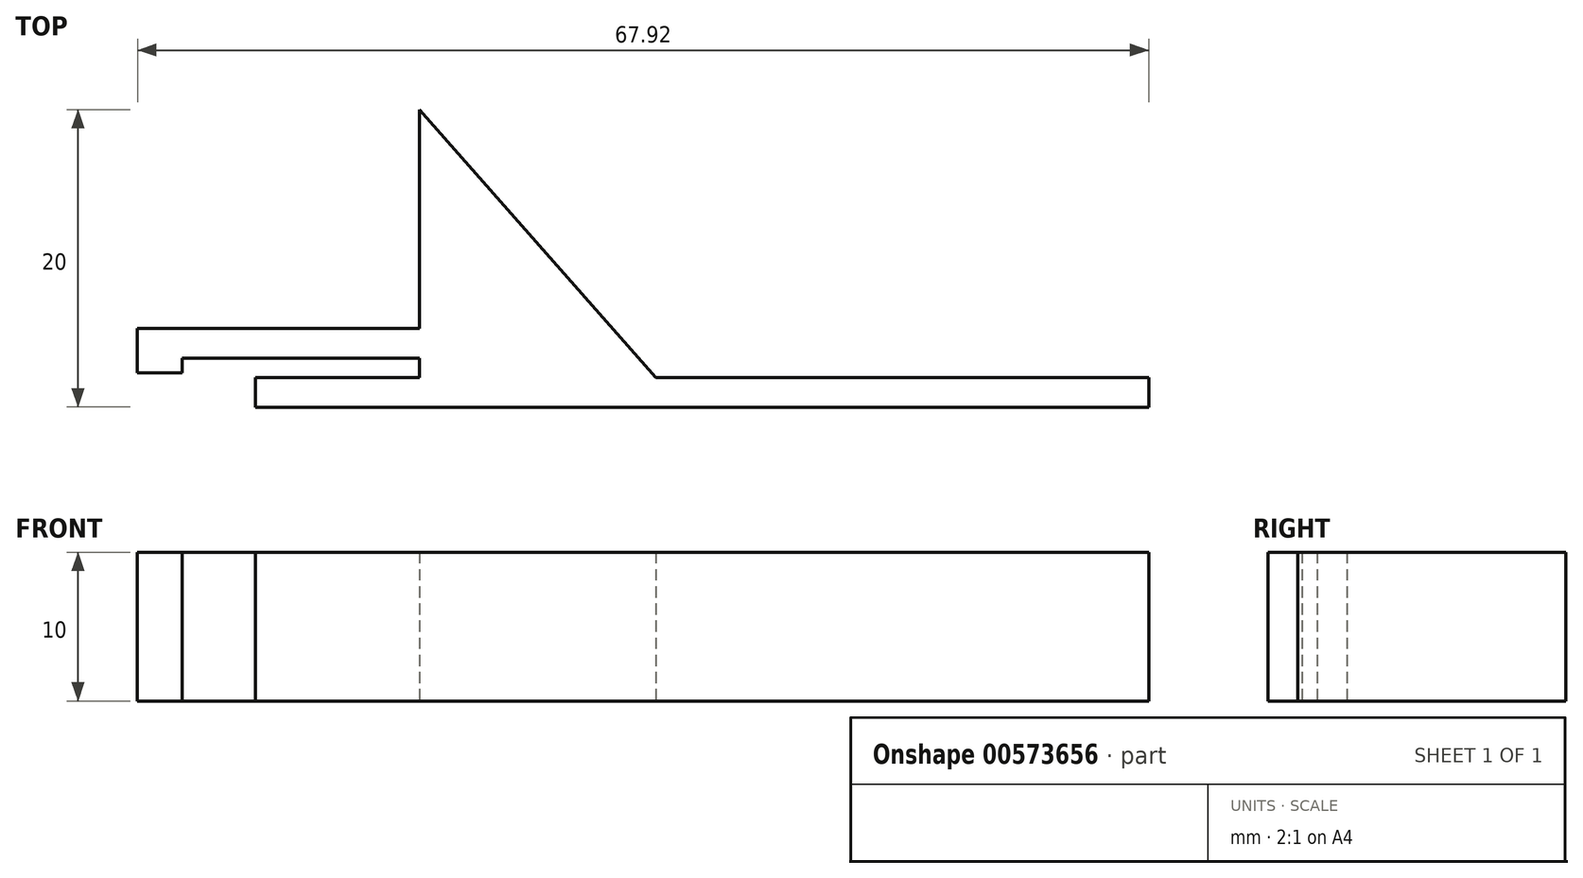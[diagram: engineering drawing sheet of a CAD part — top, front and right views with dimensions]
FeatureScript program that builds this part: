
annotation { "Feature Type Name" : "Feature", "Feature Type Description" : "" }
export const myFeature = defineFeature(function(context is Context, id is Id, definition is map)
    precondition{}
    {
        {
            var Q0;
            Q0=qCreatedBy(makeId("Top.planeOp"),FACE);
            var sketch = newSketch(context, id + "F0", { "sketchPlane" : qUnion([Q0])});
            skLineSegment(sketch, "E0", {"start": v(-11, 1.8) * mm, "end": v(49, 1.8) * mm});
            skLineSegment(sketch, "E1", {"start": v(49, 1.8) * mm, "end": v(49, 3.8) * mm});
            skLineSegment(sketch, "E2", {"start": v(49.2, 3.8) * mm, "end": v(15.9, 3.8) * mm});
            skLineSegment(sketch, "E3", {"start": v(-11, 1.8) * mm, "end": v(-11, 3.8) * mm});
            skLineSegment(sketch, "E4", {"start": v(-11, 3.8) * mm, "end": v(0, 3.8) * mm});
            skLineSegment(sketch, "E5", {"start": v(0, 5.1) * mm, "end": v(-15.92, 5.1) * mm});
            skLineSegment(sketch, "E6", {"start": v(-15.92, 5.1) * mm, "end": v(-15.92, 4.1) * mm});
            skLineSegment(sketch, "E7", {"start": v(-15.92, 4.1) * mm, "end": v(-18.92, 4.1) * mm});
            skLineSegment(sketch, "E8", {"start": v(-18.92, 4.1) * mm, "end": v(-18.92, 7.1) * mm});
            skLineSegment(sketch, "E9", {"start": v(-18.92, 7.1) * mm, "end": v(0, 7.1) * mm});
            skLineSegment(sketch, "E10", {"start": v(0, 7.1) * mm, "end": v(0, 21.8) * mm});
            skLineSegment(sketch, "E11", {"start": v(0, 21.8) * mm, "end": v(15.9, 3.8) * mm});
            skLineSegment(sketch, "E12", {"start": v(0, 3.8) * mm, "end": v(0, 5.1) * mm});
            skSolve(sketch);
        }
        {
            var Q0;
            Q0 = qSketchRegion(id + "F0", true);
            extrude(context, id + "F1", {"entities" : qUnion([Q0]), "depth" : 10 * mm, "offsetDistance" : 25 * mm});
        }
    });
